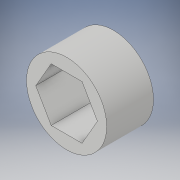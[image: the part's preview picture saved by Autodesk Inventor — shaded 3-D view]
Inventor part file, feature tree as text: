
AUTODESK INVENTOR PART (.ipt)
format: ipt  version: 2018 (Build 220112000, 112)  size: 101,888 bytes
history: native  units: in
note: dims shown in document units (in); Inventor stores cm internally (conversion verified against a paired STEP export)
features: extrude x1, sketch x1
ambient origin geometry x8: Origin, YZ Plane, XZ Plane, XY Plane, X Axis, Y Axis, Z Axis, Center Point
bodies: Solid1 (feature_tree)
feature tree (2):
  extrude  "Extrusion1"  Depth=0.4375in
  sketch  "Sketch1"  dims[d0=0.5in d1=0.75in d2=0.4375in d3=0.0in]
